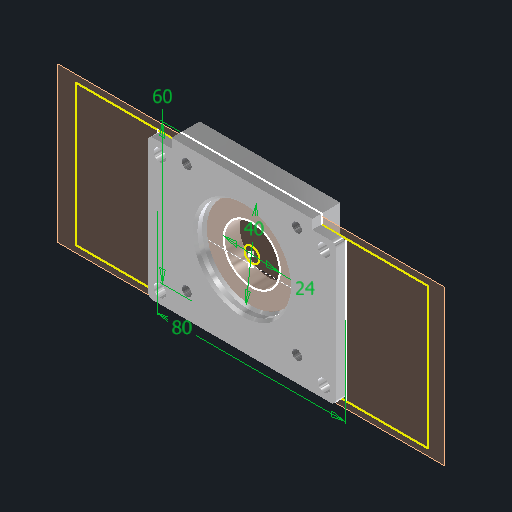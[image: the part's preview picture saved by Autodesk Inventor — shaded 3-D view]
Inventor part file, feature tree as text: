
AUTODESK INVENTOR PART (.ipt)
format: ipt  version: 2022 (Build 260153000, 153)  size: 187,904 bytes
history: native  units: mm
features: reference x10, other x5, sketch x3, chamfer x3, plane x2, extrude x2, hole x2, fillet x1
ambient origin geometry x8: Origin, YZ Plane, XZ Plane, XY Plane, X Axis, Y Axis, Z Axis, Center Point
bodies: Solid1 (feature_tree)
feature tree (28):
  plane  "Work Plane1"
  sketch  "Sketch1"  dims[d0=40.0mm d1=80.0mm]
  extrude  "Extrusion1"  Depth=80.0mm
  plane  "Work Plane2"
  extrude  "Extrusion2"  Depth=60.0mm
  hole  "Hole1"  [1 undecoded]
  hole  "Hole2"  [1 undecoded]
  fillet  "Fillet1"  Radius=4.0mm
  chamfer  "Chamfer1"  Distance=2.0mm
  chamfer  "Chamfer2"  Distance=2.0mm Angle=45.0deg
  chamfer  "Chamfer3"  Distance=24.0mm
  reference  "Reference1"
  reference  "Reference2"
  reference  "Reference3"
  reference  "Reference4"
  reference  "Reference5"
  reference  "Reference6"
  sketch  "Sketch2"  dims[d2=4.0mm d3=0.0mm d4=60.0mm]
  reference  "Reference7"
  reference  "Reference8"
  reference  "Reference9"
  reference  "Reference10"
  sketch  "Sketch3"  dims[d5=8.0mm d6=0.0mm d7=4.134mm d8=8.0mm d9=10.4mm d10=2.0mm d11=90.0deg d12=10.0mm d13=20.594885mm d14=70.0mm d15=50.0mm d16=5.3mm d17=10.0mm d18=10.4mm d19=2.0mm d20=90.0deg d21=12.8mm d22=20.594885mm d23=4.0mm d24=2.0mm d25=1.0mm d26=2.0mm d27=45.0deg d28=24.0mm d29=1.0mm d30=2.0mm d31=45.0deg d32=1.0mm d33=2.0mm d34=45.0deg]
  other  "SistemaDeElevación.iam"
  other  "soporte de rodamientos:1"
  other  "NEMA 23 - 76mm:1"
  other  "Bevel Gears:1"
  other  "Bevel Gear2:1"
note: 2 required parameter values undecoded (feature->parameter linkage not recoverable at this tier; creation-order binding heuristic only, values carry confidence <= 0.55)
